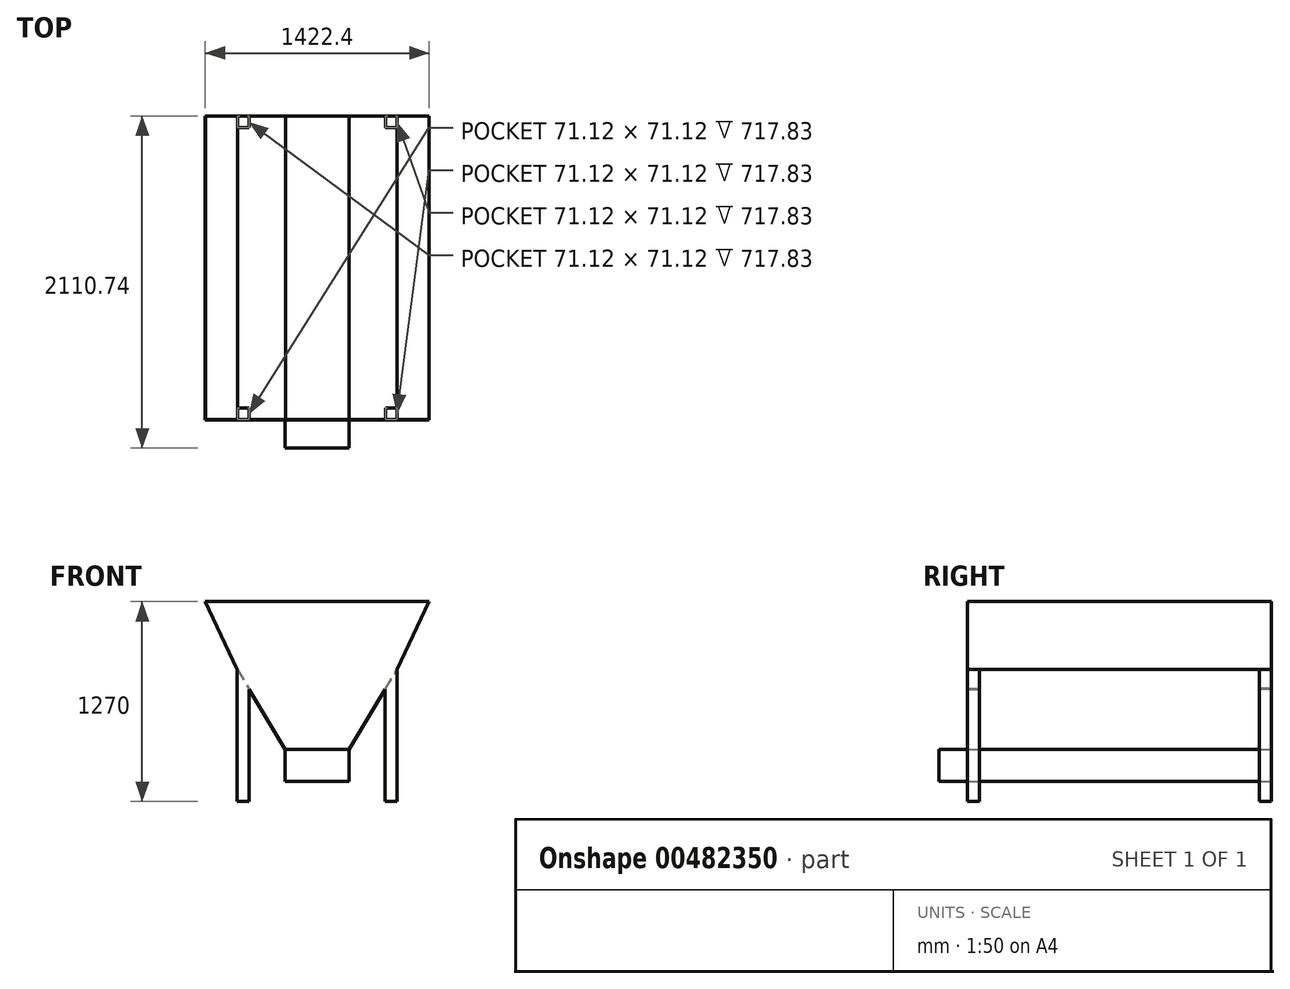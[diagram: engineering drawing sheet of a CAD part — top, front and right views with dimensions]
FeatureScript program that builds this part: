
annotation { "Feature Type Name" : "Feature", "Feature Type Description" : "" }
export const myFeature = defineFeature(function(context is Context, id is Id, definition is map)
    precondition{}
    {
        {
            var Q0;
            Q0=qCreatedBy(makeId("Front.planeOp"),FACE);
            var sketch = newSketch(context, id + "F0", { "sketchPlane" : qUnion([Q0])});
            skLineSegment(sketch, "E0", {"start": v(0, 0) * mm, "end": v(-203.2, 0) * mm});
            skLineSegment(sketch, "E1", {"start": v(-203.2, 0) * mm, "end": v(-203.2, 203.2) * mm});
            skLineSegment(sketch, "E2", {"start": v(-203.2, 203.2) * mm, "end": v(-508, 711.2) * mm});
            skLineSegment(sketch, "E3", {"start": v(-508, 711.2) * mm, "end": v(-711.2, 1143) * mm});
            skLineSegment(sketch, "E4", {"start": v(-711.2, 1143) * mm, "end": v(0, 1143) * mm});
            skLineSegment(sketch, "E5", {"start": v(0, 0) * mm, "end": v(0, -218.09) * mm, "construction": true});
            skLineSegment(sketch, "E6.MirrorCS", {"start": v(203.2, 203.2) * mm, "end": v(508, 711.2) * mm});
            skLineSegment(sketch, "E7.MirrorCS", {"start": v(0, 0) * mm, "end": v(203.2, 0) * mm});
            skLineSegment(sketch, "E8.MirrorCS", {"start": v(203.2, 0) * mm, "end": v(203.2, 203.2) * mm});
            skLineSegment(sketch, "E9.MirrorCS", {"start": v(508, 711.2) * mm, "end": v(711.2, 1143) * mm});
            skLineSegment(sketch, "E10.MirrorCS", {"start": v(711.2, 1143) * mm, "end": v(0, 1143) * mm});
            skSolve(sketch);
        }
        {
            var Q0;
            Q0 = qSketchRegion(id + "F0", true);
            extrude(context, id + "F1", {"entities" : qUnion([Q0]), "depth" : 1930.4 * mm, "offsetDistance" : 25.4 * mm});
        }
        {
            var Q0;
            Q0=makeQuery(id+"F1.opExtrude","SWEPT_FACE",FACE,{"disambiguationData":[OSD([sQuery(id+"F0.wireOp",EDGE,"E0"),sQuery(id+"F0.wireOp",EDGE,"E7.MirrorCS")])]});
            cPlane(context, id + "F2", {"entities" : qUnion([Q0]), "cplaneType" : CPlaneType.OFFSET, "offset" : 127 * mm, "width" : 152.4 * mm, "height" : 152.4 * mm});
        }
        {
            var Q0;
            Q0=qCreatedBy(id+"F2.planeOp",FACE);
            var sketch = newSketch(context, id + "F3", { "sketchPlane" : qUnion([Q0])});
            skLineSegment(sketch, "E11.bottom", {"start": v(-431.8, 1854.2) * mm, "end": v(-508, 1854.2) * mm});
            skLineSegment(sketch, "E11.top", {"start": v(-431.8, 1930.4) * mm, "end": v(-508, 1930.4) * mm});
            skLineSegment(sketch, "E11.left", {"start": v(-431.8, 1854.2) * mm, "end": v(-431.8, 1930.4) * mm});
            skLineSegment(sketch, "E11.right", {"start": v(-508, 1854.2) * mm, "end": v(-508, 1930.4) * mm});
            skLineSegment(sketch, "E12.bottom", {"start": v(431.8, 1854.2) * mm, "end": v(508, 1854.2) * mm});
            skLineSegment(sketch, "E12.top", {"start": v(431.8, 1930.4) * mm, "end": v(508, 1930.4) * mm});
            skLineSegment(sketch, "E12.left", {"start": v(431.8, 1854.2) * mm, "end": v(431.8, 1930.4) * mm});
            skLineSegment(sketch, "E12.right", {"start": v(508, 1854.2) * mm, "end": v(508, 1930.4) * mm});
            skLineSegment(sketch, "E13.bottom", {"start": v(431.8, 76.2) * mm, "end": v(508, 76.2) * mm});
            skLineSegment(sketch, "E13.top", {"start": v(431.8, 0) * mm, "end": v(508, 0) * mm});
            skLineSegment(sketch, "E13.left", {"start": v(431.8, 76.2) * mm, "end": v(431.8, 0) * mm});
            skLineSegment(sketch, "E13.right", {"start": v(508, 76.2) * mm, "end": v(508, 0) * mm});
            skLineSegment(sketch, "E14.bottom", {"start": v(-431.8, 76.2) * mm, "end": v(-508, 76.2) * mm});
            skLineSegment(sketch, "E14.top", {"start": v(-431.8, 0) * mm, "end": v(-508, 0) * mm});
            skLineSegment(sketch, "E14.left", {"start": v(-431.8, 76.2) * mm, "end": v(-431.8, 0) * mm});
            skLineSegment(sketch, "E14.right", {"start": v(-508, 76.2) * mm, "end": v(-508, 0) * mm});
            skSolve(sketch);
        }
        {
            var Q0;
            Q0 = qSketchRegion(id + "F3", true);
            extrude(context, id + "F4", {"entities" : qUnion([Q0]), "operationType" : NewBodyOperationType.ADD, "endBound" : BoundingType.UP_TO_NEXT, "oppositeDirection" : true, "depth" : 25.4 * mm, "offsetDistance" : 25.4 * mm});
        }
        {
            var Q0;
            Q0=makeQuery(id+"F4.boolean.opBoolean","MERGE",FACE,{"derivedFrom":[makeQuery(id+"F1.opExtrude","CAP_FACE",FACE,{"disambiguationData":[OSD([sQuery(id+"F0.wireOp",EDGE,"E0"),sQuery(id+"F0.wireOp",EDGE,"E1"),sQuery(id+"F0.wireOp",EDGE,"E2"),sQuery(id+"F0.wireOp",EDGE,"E3"),sQuery(id+"F0.wireOp",EDGE,"E4"),sQuery(id+"F0.wireOp",EDGE,"E6.MirrorCS"),sQuery(id+"F0.wireOp",EDGE,"E7.MirrorCS"),sQuery(id+"F0.wireOp",EDGE,"E8.MirrorCS"),sQuery(id+"F0.wireOp",EDGE,"E9.MirrorCS"),sQuery(id+"F0.wireOp",EDGE,"E10.MirrorCS")])],"isStart":false}),makeQuery(id+"F4.opExtrude","SWEPT_FACE",FACE,{"disambiguationData":[OSD([sQuery(id+"F3.wireOp",EDGE,"E11.top")])]}),makeQuery(id+"F4.opExtrude","SWEPT_FACE",FACE,{"disambiguationData":[OSD([sQuery(id+"F3.wireOp",EDGE,"E12.top")])]})]});
            var sketch = newSketch(context, id + "F5", { "sketchPlane" : qUnion([Q0])});
            skLineSegment(sketch, "E15.bottom", {"start": v(-203.2, 0) * mm, "end": v(203.2, 0) * mm});
            skLineSegment(sketch, "E15.top", {"start": v(-203.2, 203.2) * mm, "end": v(203.2, 203.2) * mm});
            skLineSegment(sketch, "E15.left", {"start": v(-203.2, 0) * mm, "end": v(-203.2, 203.2) * mm});
            skLineSegment(sketch, "E15.right", {"start": v(203.2, 0) * mm, "end": v(203.2, 203.2) * mm});
            skSolve(sketch);
        }
        {
            var Q0;
            Q0 = qSketchRegion(id + "F5", true);
            extrude(context, id + "F6", {"entities" : qUnion([Q0]), "operationType" : NewBodyOperationType.ADD, "depth" : 180.34 * mm, "offsetDistance" : 25.4 * mm});
        }
        {
            var Q0;
            Q0=makeQuery(id+"F1.opExtrude","SWEPT_FACE",FACE,{"disambiguationData":[OSD([sQuery(id+"F0.wireOp",EDGE,"E4"),sQuery(id+"F0.wireOp",EDGE,"E10.MirrorCS")])]});
            shell(context, id + "F7", {"entities" : qUnion([Q0]), "thickness" : 2.54 * mm});
        }
    });
